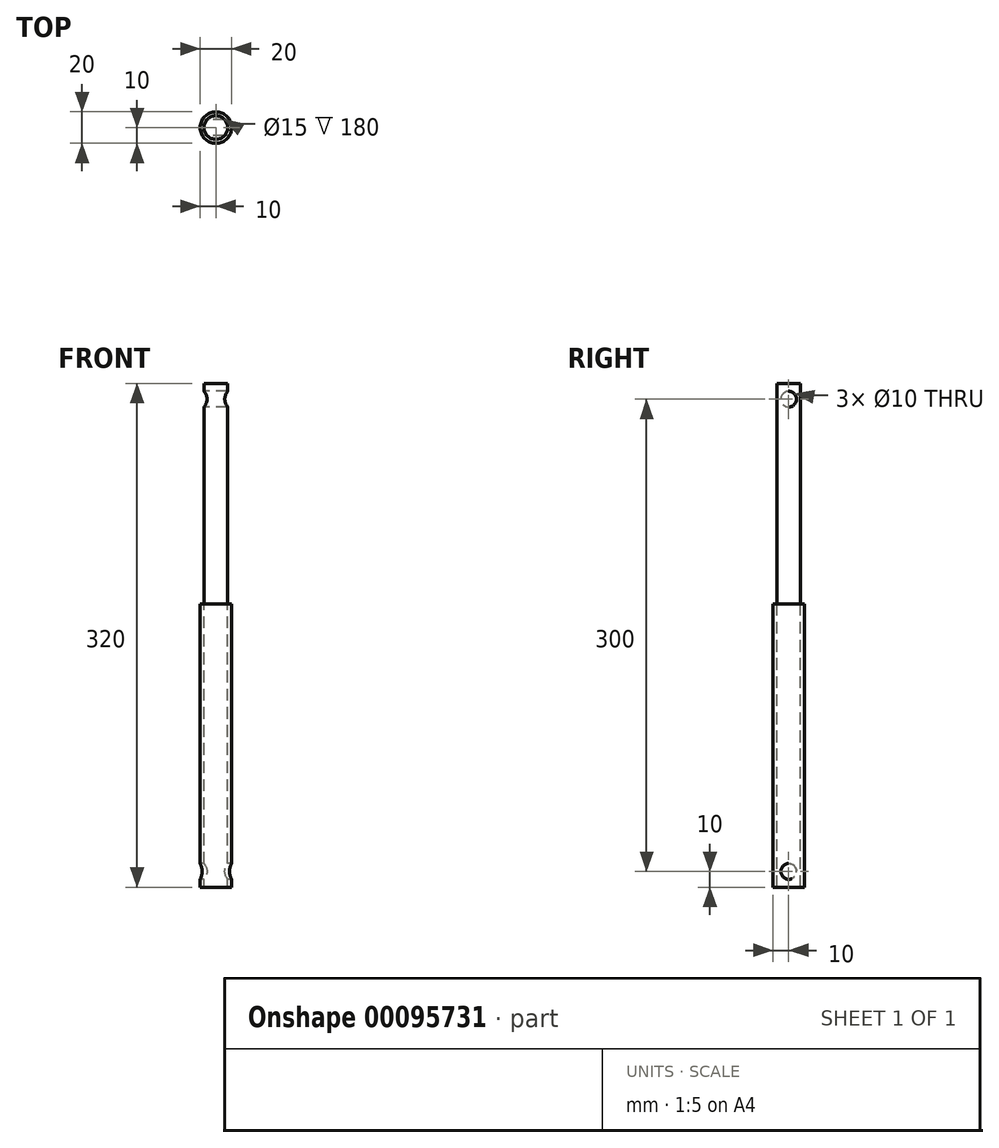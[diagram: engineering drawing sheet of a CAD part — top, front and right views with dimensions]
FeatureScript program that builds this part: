
annotation { "Feature Type Name" : "Feature", "Feature Type Description" : "" }
export const myFeature = defineFeature(function(context is Context, id is Id, definition is map)
    precondition{}
    {
        {
            var Q0;
            Q0=qCreatedBy(makeId("Top.planeOp"),FACE);
            var sketch = newSketch(context, id + "F0", { "sketchPlane" : qUnion([Q0])});
            skCircle(sketch, "E0", {"center": v(0, 0) * mm, "radius": 7.5 * mm});
            skSolve(sketch);
        }
        {
            var Q0;
            Q0=makeQuery(id+"F0.imprint","IMPRINT",FACE,{"disambiguationData":[TD([[makeQuery(id+"F0.imprint","IMPRINT",EDGE,{"derivedFrom":sQuery(id+"F0.wireOp",EDGE,"E0")}),1.0]])]});
            extrude(context, id + "F1", {"entities" : qUnion([Q0]), "depth" : 140 * mm});
        }
        {
            var Q0;
            Q0=qCreatedBy(makeId("Right.planeOp"),FACE);
            var sketch = newSketch(context, id + "F2", { "sketchPlane" : qUnion([Q0])});
            skCircle(sketch, "E1", {"center": v(0, 130) * mm, "radius": 5 * mm});
            skSolve(sketch);
        }
        {
            var Q0;
            Q0 = qSketchRegion(id + "F2", true);
            extrude(context, id + "F3", {"entities" : qUnion([Q0]), "operationType" : NewBodyOperationType.REMOVE, "endBound" : BoundingType.UP_TO_NEXT, "depth" : 16 * mm, "hasSecondDirection" : true, "secondDirectionBound" : SecondDirectionBoundingType.UP_TO_NEXT, "secondDirectionOppositeDirection" : true, "secondDirectionDepth" : 25 * mm});
        }
        {
            var Q0;
            Q0=qCreatedBy(makeId("Top.planeOp"),FACE);
            var sketch = newSketch(context, id + "F4", { "sketchPlane" : qUnion([Q0])});
            skCircle(sketch, "E2", {"center": v(0, 0) * mm, "radius": 10 * mm});
            skCircle(sketch, "E3", {"center": v(0, 0) * mm, "radius": 7.5 * mm});
            skSolve(sketch);
        }
        {
            var Q0;
            Q0 = qSketchRegion(id + "F4", true);
            extrude(context, id + "F5", {"entities" : qUnion([Q0]), "oppositeDirection" : true, "depth" : 180 * mm});
        }
        {
            var Q0;
            Q0=qCreatedBy(makeId("Right.planeOp"),FACE);
            var sketch = newSketch(context, id + "F6", { "sketchPlane" : qUnion([Q0])});
            skCircle(sketch, "E4", {"center": v(0, -170) * mm, "radius": 5 * mm});
            skSolve(sketch);
        }
        {
            var Q0;
            Q0 = qSketchRegion(id + "F6", true);
            extrude(context, id + "F7", {"entities" : qUnion([Q0]), "operationType" : NewBodyOperationType.REMOVE, "depth" : 20 * mm, "hasSecondDirection" : true, "secondDirectionOppositeDirection" : true, "secondDirectionDepth" : 20 * mm});
        }
    });
